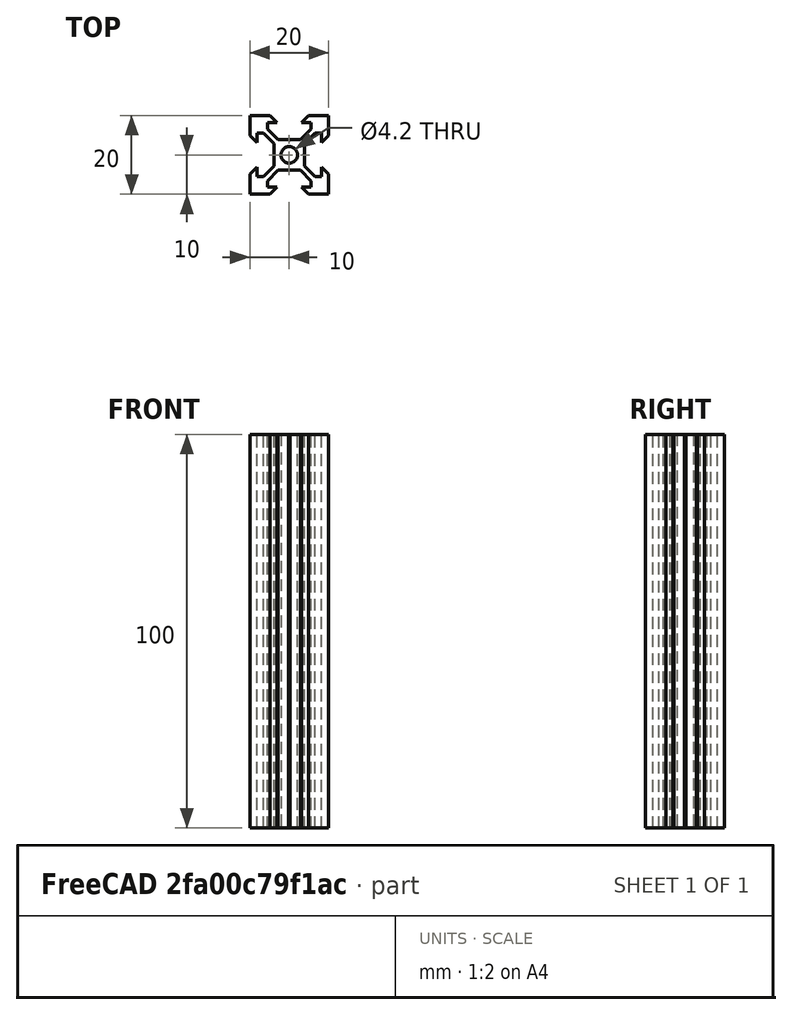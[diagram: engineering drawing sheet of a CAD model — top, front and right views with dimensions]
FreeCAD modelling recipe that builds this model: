
FCSTD DOCUMENT  (FreeCAD 0.19R24267 +99 (Git))
Label: Vslot 2020 Parametrique
License: All rights reserved
LicenseURL: http://en.wikipedia.org/wiki/All_rights_reserved
objects: Spreadsheet::Sheet×1, Sketcher::SketchObject×1, PartDesign::Pad×1, PartDesign::Body×1, App::Part×1
note: 4 computed .brp shape members not serialized (recipe doc carries the construction recipe); baked Part::Feature solids carry a one-line shape summary decoded from their .brp

FEATURE [Spreadsheet::Sheet] Spreadsheet  label="VSlot_longeur"
  cells = A1=Longeur en mm; B1(VSOL_L)=100
FEATURE [Sketcher::SketchObject] Sketch
  FullyConstrained = false
  MapMode = 5
  Support = -> [XY_Plane001]
  sketch-geometry (57):
    g0: Circle CenterX=0 CenterY=0 CenterZ=0 NormalX=0 NormalY=0 NormalZ=1 AngleXU=0 Radius=2.1
    g1: LineSegment StartX=0 StartY=-3.69157 StartZ=0 EndX=0.174924 EndY=-3.89157 EndZ=0
    g2: LineSegment StartX=0.174924 StartY=-3.89157 StartZ=0 EndX=2.84 EndY=-3.89157 EndZ=0
    g3: LineSegment StartX=2.84 StartY=-3.89157 StartZ=0 EndX=5.53504 EndY=-6.58661 EndZ=0
    g4: LineSegment StartX=5.53504 StartY=-6.58661 StartZ=0 EndX=5.53504 EndY=-8.2 EndZ=0
    g5: LineSegment StartX=5.53504 StartY=-8.2 StartZ=0 EndX=3.1 EndY=-8.2 EndZ=0
    g6: LineSegment StartX=3.1 StartY=-8.2 StartZ=0 EndX=4.9 EndY=-10 EndZ=0
    g7: LineSegment StartX=4.9 StartY=-10 StartZ=0 EndX=10 EndY=-10 EndZ=0
    g8: LineSegment StartX=10 StartY=-10 StartZ=0 EndX=10 EndY=-4.9 EndZ=0
    g9: LineSegment StartX=10 StartY=-4.9 StartZ=0 EndX=8.2 EndY=-3.1 EndZ=0
    g10: LineSegment StartX=8.2 StartY=-3.1 StartZ=0 EndX=8.2 EndY=-5.53504 EndZ=0
    g11: LineSegment StartX=8.2 StartY=-5.53504 StartZ=0 EndX=6.58661 EndY=-5.53504 EndZ=0
    g12: LineSegment StartX=6.58661 StartY=-5.53504 StartZ=0 EndX=3.89157 EndY=-2.84 EndZ=0
    g13: LineSegment StartX=3.89157 StartY=-2.84 StartZ=0 EndX=3.89157 EndY=-0.174924 EndZ=0
    g14: LineSegment StartX=3.89157 StartY=-0.174924 StartZ=0 EndX=3.69157 EndY=0 EndZ=0
    g15: LineSegment StartX=-2.84 StartY=3.89157 StartZ=0 EndX=-5.49062 EndY=6.54219 EndZ=0
    g16: LineSegment StartX=-5.49062 StartY=6.54219 StartZ=0 EndX=-5.49062 EndY=8.2 EndZ=0
    g17: LineSegment StartX=-5.49062 StartY=8.2 StartZ=0 EndX=-3.1 EndY=8.2 EndZ=0
    g18: LineSegment StartX=-3.1 StartY=8.2 StartZ=0 EndX=-4.9 EndY=10 EndZ=0
    g19: LineSegment StartX=-4.9 StartY=10 StartZ=0 EndX=-10 EndY=10 EndZ=0
    g20: LineSegment StartX=-10 StartY=10 StartZ=0 EndX=-10 EndY=4.9 EndZ=0
    g21: LineSegment StartX=-10 StartY=4.9 StartZ=0 EndX=-8.2 EndY=3.1 EndZ=0
    g22: LineSegment StartX=-8.2 StartY=3.1 StartZ=0 EndX=-8.2 EndY=5.49062 EndZ=0
    g23: LineSegment StartX=-8.2 StartY=5.49062 StartZ=0 EndX=-6.54219 EndY=5.49062 EndZ=0
    g24: LineSegment StartX=-6.54219 StartY=5.49062 StartZ=0 EndX=-3.89157 EndY=2.84 EndZ=0
    g25: LineSegment StartX=-3.89157 StartY=2.84 StartZ=0 EndX=-3.89157 EndY=0.219864 EndZ=0
    g26: LineSegment StartX=-3.89157 StartY=0.219864 StartZ=0 EndX=-3.69157 EndY=0 EndZ=0
    g27: LineSegment StartX=-0.219864 StartY=3.89157 StartZ=0 EndX=-2.84 EndY=3.89157 EndZ=0
    g28: LineSegment StartX=0 StartY=3.69157 StartZ=0 EndX=-0.219864 EndY=3.89157 EndZ=0
    g29: LineSegment StartX=0 StartY=3.69157 StartZ=0 EndX=0.170281 EndY=3.89157 EndZ=0
    g30: LineSegment StartX=0.170281 StartY=3.89157 StartZ=0 EndX=2.84 EndY=3.89157 EndZ=0
    g31: LineSegment StartX=2.84 StartY=3.89157 StartZ=0 EndX=5.52467 EndY=6.57624 EndZ=0
    g32: LineSegment StartX=5.52467 StartY=6.57624 StartZ=0 EndX=5.52467 EndY=8.2 EndZ=0
    g33: LineSegment StartX=5.52467 StartY=8.2 StartZ=0 EndX=3.1 EndY=8.2 EndZ=0
    g34: LineSegment StartX=3.1 StartY=8.2 StartZ=0 EndX=4.9 EndY=10 EndZ=0
    g35: LineSegment StartX=4.9 StartY=10 StartZ=0 EndX=10 EndY=10 EndZ=0
    g36: LineSegment StartX=10 StartY=10 StartZ=0 EndX=10 EndY=4.9 EndZ=0
    g37: LineSegment StartX=10 StartY=4.9 StartZ=0 EndX=8.2 EndY=3.1 EndZ=0
    g38: LineSegment StartX=8.2 StartY=3.1 StartZ=0 EndX=8.2 EndY=5.52467 EndZ=0
    g39: LineSegment StartX=8.2 StartY=5.52467 StartZ=0 EndX=6.57624 EndY=5.52467 EndZ=0
    g40: LineSegment StartX=6.57624 StartY=5.52467 StartZ=0 EndX=3.89157 EndY=2.84 EndZ=0
    g41: LineSegment StartX=3.89157 StartY=2.84 StartZ=0 EndX=3.89157 EndY=0.170281 EndZ=0
    g42: LineSegment StartX=3.89157 StartY=0.170281 StartZ=0 EndX=3.69157 EndY=0 EndZ=0
    g43: LineSegment StartX=0 StartY=-3.69157 StartZ=0 EndX=-0.224285 EndY=-3.89157 EndZ=0
    g44: LineSegment StartX=-0.224285 StartY=-3.89157 StartZ=0 EndX=-2.84 EndY=-3.89157 EndZ=0
    g45: LineSegment StartX=-2.84 StartY=-3.89157 StartZ=0 EndX=-5.53618 EndY=-6.58775 EndZ=0
    g46: LineSegment StartX=-5.53618 StartY=-6.58775 StartZ=0 EndX=-5.53618 EndY=-8.2 EndZ=0
    g47: LineSegment StartX=-5.53618 StartY=-8.2 StartZ=0 EndX=-3.1 EndY=-8.2 EndZ=0
    g48: LineSegment StartX=-3.1 StartY=-8.2 StartZ=0 EndX=-4.9 EndY=-10 EndZ=0
    g49: LineSegment StartX=-4.9 StartY=-10 StartZ=0 EndX=-10 EndY=-10 EndZ=0
    g50: LineSegment StartX=-10 StartY=-10 StartZ=0 EndX=-10 EndY=-4.9 EndZ=0
    g51: LineSegment StartX=-10 StartY=-4.9 StartZ=0 EndX=-8.2 EndY=-3.1 EndZ=0
    g52: LineSegment StartX=-8.2 StartY=-3.1 StartZ=0 EndX=-8.2 EndY=-5.53618 EndZ=0
    g53: LineSegment StartX=-8.2 StartY=-5.53618 StartZ=0 EndX=-6.58775 EndY=-5.53618 EndZ=0
    g54: LineSegment StartX=-6.58775 StartY=-5.53618 StartZ=0 EndX=-3.89157 EndY=-2.84 EndZ=0
    g55: LineSegment StartX=-3.89157 StartY=-2.84 StartZ=0 EndX=-3.89157 EndY=-0.224285 EndZ=0
    g56: LineSegment StartX=-3.89157 StartY=-0.224285 StartZ=0 EndX=-3.69157 EndY=0 EndZ=0
  constraints (152):
    c: Coincident(g0,g-1)
    c: Radius(g0) = 2.1
    c: PointOnObject(g1,g-2)
    c: Coincident(g1,g2)
    c: Horizontal(g2)
    c: Coincident(g2,g3)
    c: Coincident(g3,g4)
    c: Vertical(g4)
    c: Coincident(g4,g5)
    c: Horizontal(g5)
    c: Coincident(g5,g6)
    c: Coincident(g6,g7)
    c: Horizontal(g7)
    c: Coincident(g7,g8)
    c: Vertical(g8)
    c: Coincident(g8,g9)
    c: Coincident(g9,g10)
    c: Vertical(g10)
    c: Coincident(g10,g11)
    c: Horizontal(g11)
    c: Coincident(g11,g12)
    c: Coincident(g12,g13)
    c: Coincident(g13,g14)
    c: PointOnObject(g14,g-1)
    c: Parallel(g6,g9)
    c: Parallel(g3,g12)
    c: Equal(g2,g13)
    c: Equal(g3,g12)
    c: Equal(g6,g9)
    c: Equal(g4,g11)
    c: Equal(g5,g10)
    c: Equal(g7,g8)
    c: Equal(g1,g14)
    c: Parallel(g3,g6)
    c: Coincident(g28,g27)
    c: Horizontal(g27)
    c: Coincident(g27,g15)
    c: Coincident(g15,g16)
    c: Vertical(g16)
    c: Coincident(g16,g17)
    c: Horizontal(g17)
    c: Coincident(g17,g18)
    c: Coincident(g18,g19)
    c: Horizontal(g19)
    c: Coincident(g19,g20)
    c: Vertical(g20)
    c: Coincident(g20,g21)
    c: Coincident(g21,g22)
    c: Vertical(g22)
    c: Coincident(g22,g23)
    c: Horizontal(g23)
    c: Coincident(g23,g24)
    c: Coincident(g24,g25)
    c: Coincident(g25,g26)
    c: Parallel(g18,g21)
    c: Parallel(g15,g24)
    c: Equal(g27,g25)
    c: Equal(g15,g24)
    c: Equal(g18,g21)
    c: Equal(g16,g23)
    c: Equal(g17,g22)
    c: Equal(g19,g20)
    c: Equal(g28,g26)
    c: Parallel(g15,g18)
    c: Coincident(g29,g30)
    c: Coincident(g30,g31)
    c: Coincident(g31,g32)
    c: Vertical(g32)
    c: Coincident(g32,g33)
    c: Coincident(g33,g34)
    c: Coincident(g34,g35)
    c: Horizontal(g35)
    c: Coincident(g35,g36)
    c: Vertical(g36)
    c: Coincident(g36,g37)
    c: Coincident(g37,g38)
    c: Coincident(g38,g39)
    c: Horizontal(g39)
    c: Coincident(g39,g40)
    c: Coincident(g40,g41)
    c: Coincident(g41,g42)
    c: Parallel(g34,g37)
    c: Parallel(g31,g40)
    c: Equal(g30,g41)
    c: Equal(g31,g40)
    c: Equal(g34,g37)
    c: Equal(g32,g39)
    c: Equal(g33,g38)
    c: Equal(g35,g36)
    c: Equal(g29,g42)
    c: Parallel(g31,g34)
    c: Coincident(g43,g44)
    c: Coincident(g44,g45)
    c: Coincident(g45,g46)
    c: Vertical(g46)
    c: Coincident(g46,g47)
    c: Coincident(g47,g48)
    c: Coincident(g48,g49)
    c: Horizontal(g49)
    c: Coincident(g49,g50)
    c: Vertical(g50)
    c: Coincident(g50,g51)
    c: Coincident(g51,g52)
    c: Coincident(g52,g53)
    c: Horizontal(g53)
    c: Coincident(g53,g54)
    c: Coincident(g54,g55)
    c: Coincident(g55,g56)
    c: Parallel(g48,g51)
    c: Parallel(g45,g54)
    c: Equal(g44,g55)
    c: Equal(g45,g54)
    c: Equal(g48,g51)
    c: Equal(g46,g53)
    c: Equal(g47,g52)
    c: Equal(g49,g50)
    c: Equal(g43,g56)
    c: Parallel(g45,g48)
    c: DistanceX(g49,g7) = 20
    c: DistanceY(g7,g35) = 20
    c: DistanceY(g49,g19) = 20
    c: DistanceX(g19,g35) = 20
    c: DistanceY(g54,g24) = 5.68
    c: DistanceX(g15,g30) = 5.68
    c: Coincident(g26,g56)
    c: PointOnObject(g26,g-1)
    c: Tangent(g25,g55)
    c: DistanceX(g55,g26) = 0.2
    c: Coincident(g42,g14)
    c: Tangent(g41,g13)
    c: DistanceX(g14,g41) = 0.2
    c: Symmetric(g24,g54,g-1)
    c: DistanceY(g12,g40) = 5.68
    c: Symmetric(g40,g12,g-1)
    c: Coincident(g29,g28)
    c: PointOnObject(g28,g-2)
    c: Tangent(g27,g30)
    c: Tangent(g38,g10)
    c: DistanceX(g37,g36) = 1.8
    c: Tangent(g17,g33)
    c: Tangent(g22,g52)
    c: Tangent(g47,g5)
    c: Angle(g48,g6) = 1.5708
    c: DistanceY(g6,g5) = 1.8
    c: DistanceX(g50,g51) = 1.8
    c: Tangent(g44,g2)
    c: Coincident(g43,g1)
    c: Symmetric(g44,g2,g-2)
    c: DistanceY(g51,g21) = 6.2
    c: DistanceX(g17,g33) = 6.2
    c: DistanceY(g9,g37) = 6.2
    c: DistanceX(g47,g5) = 6.2
FEATURE [PartDesign::Pad] Pad
  Direction = (1,1,1)
  Length = 100
  Length2 = 100
  Profile = -> Sketch
  Type = 0
  expr: Length = <<VSlot_longeur>>.VSOL_L
FEATURE [PartDesign::Body] Body
  Group = -> [Sketch,Pad]
  Origin = -> Origin001
  Tip = -> Pad
FEATURE [App::Part] Part  label="VSLOT_2020: 100 mm"
  Group = -> [Spreadsheet,Body]
  Origin = -> Origin
  expr: Label = <<VSLOT_2020: %s>> % <<VSlot_longeur>>.VSOL_L + << mm>>
